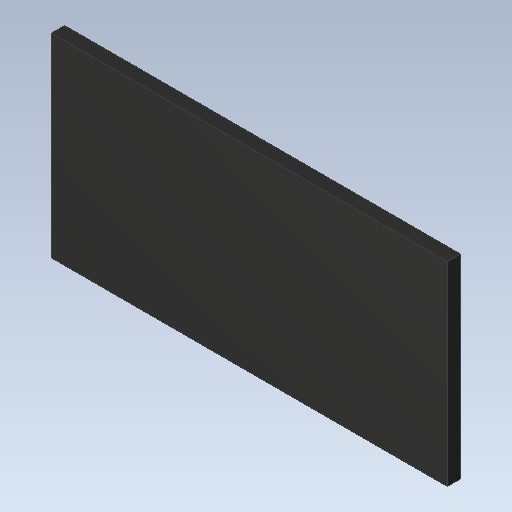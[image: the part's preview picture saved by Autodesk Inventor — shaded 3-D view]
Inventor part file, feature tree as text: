
AUTODESK INVENTOR PART (.ipt)
format: ipt  version: 2023 (Build 270158000, 158)  size: 92,160 bytes
history: imported  units: in
note: dims shown in document units (in); Inventor stores cm internally (conversion verified against a paired STEP export)
features: imported_body x1
ambient origin geometry x8: Origin, YZ Plane, XZ Plane, XY Plane, X Axis, Y Axis, Z Axis, Center Point
bodies: Solid1 (imported_parasolid), Body1 (imported_parasolid)
feature tree (1):
  imported_body  NMx_Import_Brep_tag  [imported B-rep: ~6 faces, bbox_mm=[2.9972, 1.4732, 0.1]]
